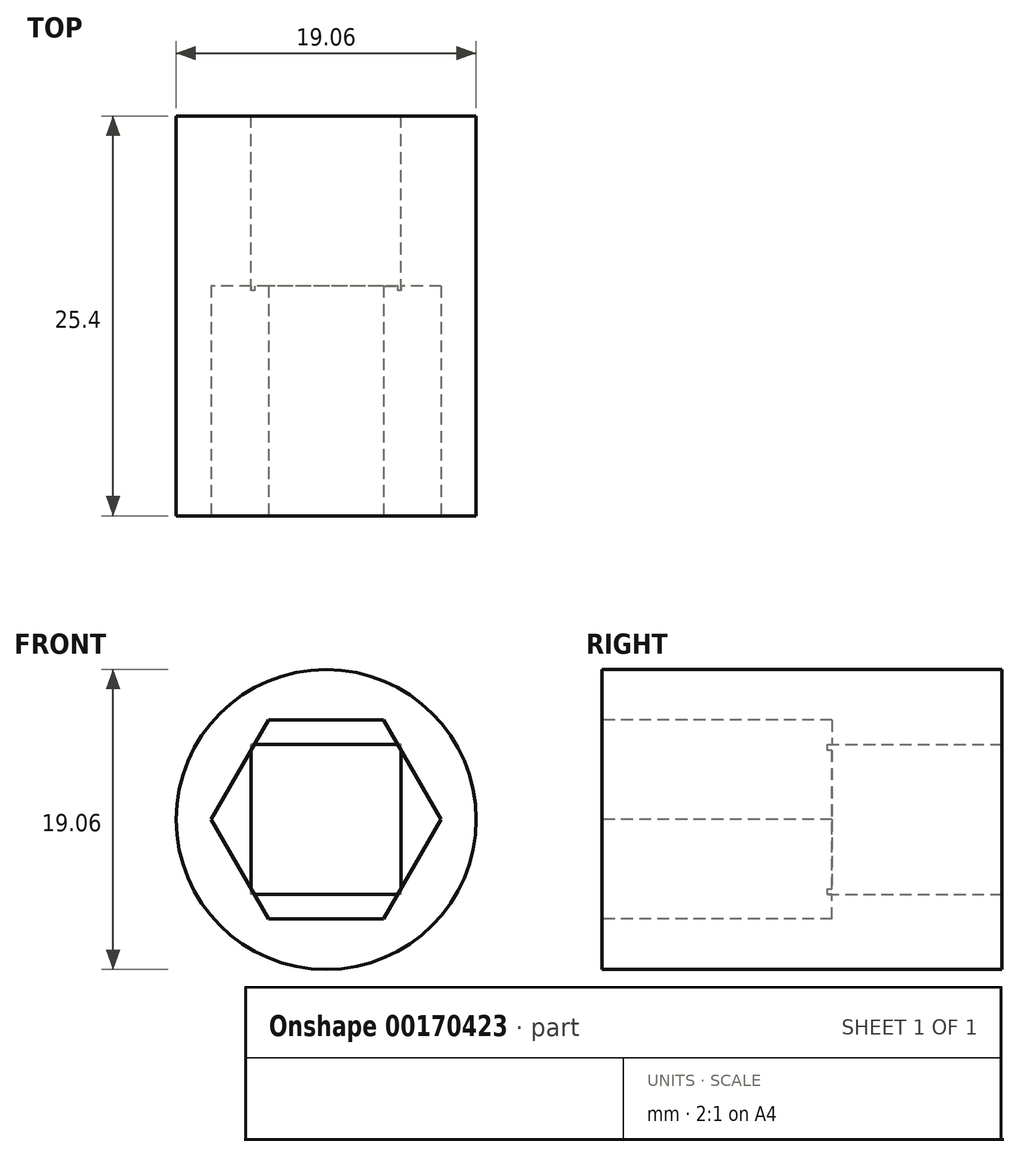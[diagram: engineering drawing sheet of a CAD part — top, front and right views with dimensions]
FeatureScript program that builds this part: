
annotation { "Feature Type Name" : "Feature", "Feature Type Description" : "" }
export const myFeature = defineFeature(function(context is Context, id is Id, definition is map)
    precondition{}
    {
        {
            var Q0;
            Q0=qCreatedBy(makeId("Front.planeOp"),FACE);
            var sketch = newSketch(context, id + "F0", { "sketchPlane" : qUnion([Q0])});
            skCircle(sketch, "E0", {"center": v(0, 0) * mm, "radius": 9.53 * mm});
            skSolve(sketch);
        }
        {
            var Q0;
            Q0 = qSketchRegion(id + "F0", true);
            extrude(context, id + "F1", {"entities" : qUnion([Q0]), "depth" : 25.4 * mm});
        }
        {
            var Q0;
            Q0=qCreatedBy(makeId("Front.planeOp"),FACE);
            var sketch = newSketch(context, id + "F2", { "sketchPlane" : qUnion([Q0])});
            skLineSegment(sketch, "E1.bottom", {"start": v(4.76, -4.76) * mm, "end": v(-4.76, -4.76) * mm});
            skLineSegment(sketch, "E1.top", {"start": v(4.76, 4.76) * mm, "end": v(-4.76, 4.76) * mm});
            skLineSegment(sketch, "E1.left", {"start": v(4.76, -4.76) * mm, "end": v(4.76, 4.76) * mm});
            skLineSegment(sketch, "E1.right", {"start": v(-4.76, -4.76) * mm, "end": v(-4.76, 4.76) * mm});
            skPoint(sketch, "E1.middle", {"position": v(0, 0) * mm});
            skCircle(sketch, "E2", {"center": v(0, 0) * mm, "radius": 4.76 * mm});
            skSolve(sketch);
        }
        {
            var Q0;
            {var subQ0=sQuery(id+"F2.wireOp",EDGE,"E2");var subQ1=makeQuery(id+"F2.imprint","INTERSECT",VERTEX,{"derivedFrom":[sQuery(id+"F2.wireOp",EDGE,"E1.top"),subQ0]});Q0=makeQuery(id+"F2.imprint","IMPRINT",FACE,{"disambiguationData":[TD([[makeQuery(id+"F2.imprint","IMPRINT",EDGE,{"disambiguationData":[TD([[subQ1,1.0]])],"derivedFrom":subQ0}),1.0]])]});}
            extrude(context, id + "F3", {"entities" : qUnion([Q0]), "operationType" : NewBodyOperationType.REMOVE, "endBound" : BoundingType.THROUGH_ALL, "depth" : 25.4 * mm});
        }
        {
            var Q0;
            Q0 = qSketchRegion(id + "F2", true);
            extrude(context, id + "F4", {"entities" : qUnion([Q0]), "operationType" : NewBodyOperationType.REMOVE, "depth" : 11.1 * mm});
        }
        {
            var Q0;
            Q0=makeQuery(id+"F1.opExtrude","CAP_FACE",FACE,{"disambiguationData":[OSD([sQuery(id+"F0.wireOp",EDGE,"E0")])],"isStart":false});
            var sketch = newSketch(context, id + "F5", { "sketchPlane" : qUnion([Q0])});
            skCircle(sketch, "E3.cCircle", {"center": v(0, 0) * mm, "radius": 6.32 * mm, "construction": true});
            skLineSegment(sketch, "E3.0", {"start": v(3.65, 6.32) * mm, "end": v(7.3, 0) * mm});
            skLineSegment(sketch, "E3.1", {"start": v(7.3, 0) * mm, "end": v(3.65, -6.32) * mm});
            skLineSegment(sketch, "E3.2", {"start": v(3.65, -6.32) * mm, "end": v(-3.65, -6.32) * mm});
            skLineSegment(sketch, "E3.3", {"start": v(-3.65, -6.32) * mm, "end": v(-7.3, 0) * mm});
            skLineSegment(sketch, "E3.4", {"start": v(-7.3, 0) * mm, "end": v(-3.65, 6.32) * mm});
            skLineSegment(sketch, "E3.5", {"start": v(-3.65, 6.32) * mm, "end": v(3.65, 6.32) * mm});
            skPoint(sketch, "E3.0.midPoint", {"position": v(5.48, 3.16) * mm});
            skSolve(sketch);
        }
        {
            var Q0;
            Q0=makeQuery(id+"F5.imprint","IMPRINT",FACE,{"disambiguationData":[TD([[makeQuery(id+"F5.imprint","IMPRINT",EDGE,{"derivedFrom":sQuery(id+"F5.wireOp",EDGE,"E3.0")}),-1.0]])]});
            extrude(context, id + "F6", {"entities" : qUnion([Q0]), "operationType" : NewBodyOperationType.REMOVE, "oppositeDirection" : true, "depth" : 14.6 * mm});
        }
    });
